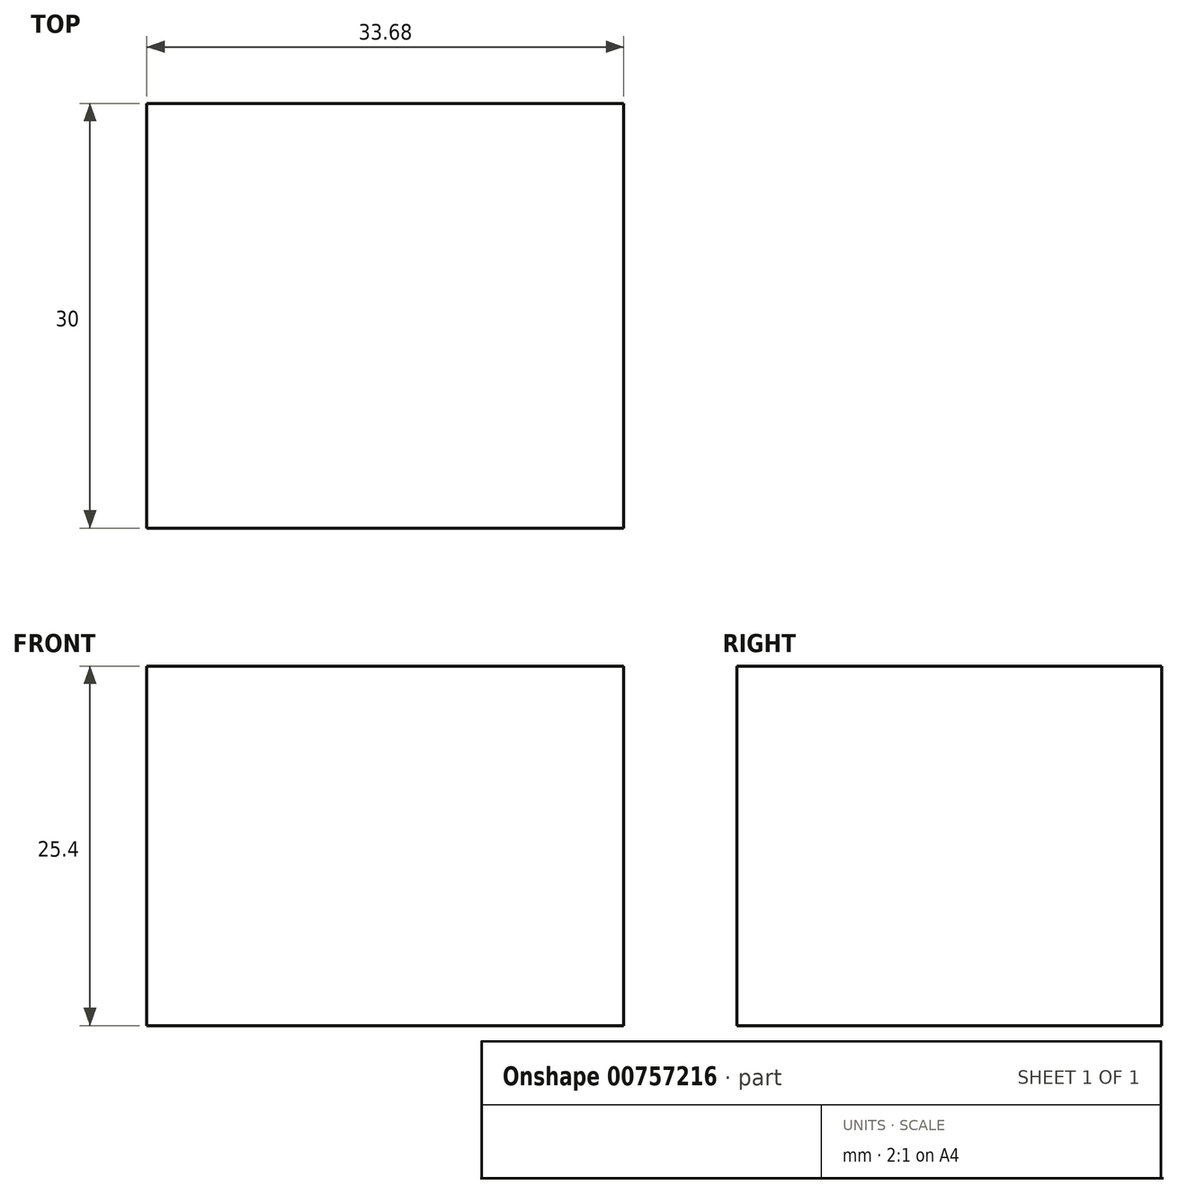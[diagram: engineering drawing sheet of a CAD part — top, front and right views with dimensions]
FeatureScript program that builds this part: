
annotation { "Feature Type Name" : "Feature", "Feature Type Description" : "" }
export const myFeature = defineFeature(function(context is Context, id is Id, definition is map)
    precondition{}
    {
        {
            var Q0;
            Q0=qCreatedBy(makeId("Top.planeOp"),FACE);
            var sketch = newSketch(context, id + "F0", { "sketchPlane" : qUnion([Q0])});
            skLineSegment(sketch, "E0.bottom", {"start": v(16.84, 15) * mm, "end": v(-16.84, 15) * mm});
            skLineSegment(sketch, "E0.top", {"start": v(16.84, -15) * mm, "end": v(-16.84, -15) * mm});
            skLineSegment(sketch, "E0.left", {"start": v(16.84, 15) * mm, "end": v(16.84, -15) * mm});
            skLineSegment(sketch, "E0.right", {"start": v(-16.84, 15) * mm, "end": v(-16.84, -15) * mm});
            skPoint(sketch, "E0.middle", {"position": v(0, 0) * mm});
            skSolve(sketch);
        }
        {
            var Q0;
            Q0=makeQuery(id+"F0.imprint","IMPRINT",FACE,{"disambiguationData":[TD([[makeQuery(id+"F0.imprint","IMPRINT",EDGE,{"derivedFrom":sQuery(id+"F0.wireOp",EDGE,"E0.bottom")}),1.0]])]});
            extrude(context, id + "F1", {"entities" : qUnion([Q0]), "depth" : 25.4 * mm, "offsetDistance" : 25.4 * mm});
        }
    });
